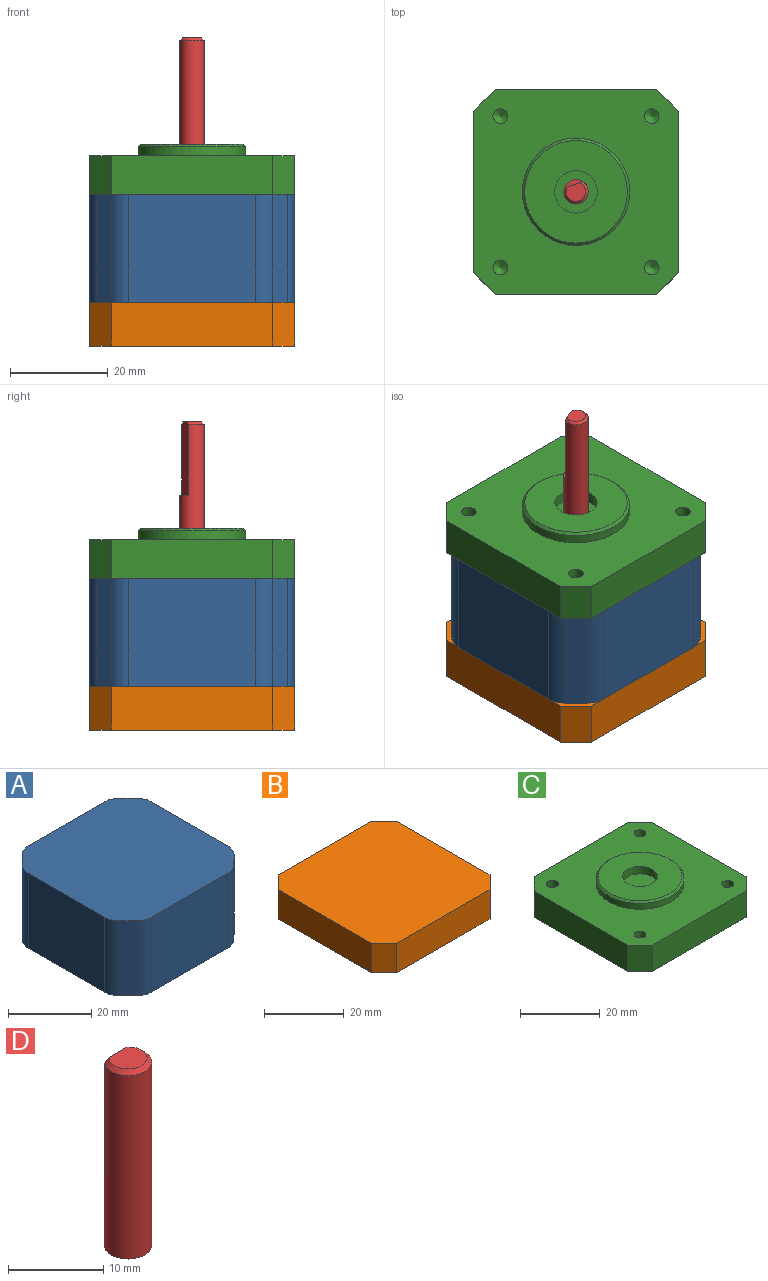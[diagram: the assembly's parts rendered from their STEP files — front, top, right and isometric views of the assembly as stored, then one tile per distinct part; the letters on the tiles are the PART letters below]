
ASSEMBLY  parts=4 mates=3
PART A: 18 faces, bbox 42x42x22 mm
  f0: plane 25.86x22mm, normal (1,0,0), area 568.9mm2, adj f4,f5,f16,f17
  f1: plane 25.86x22mm, normal (0,1,0), area 568.9mm2, adj f4,f5,f12,f13
  f2: plane 25.86x22mm, normal (-1,0,0), area 568.9mm2, adj f4,f5,f10,f11
  f3: plane 25.86x22mm, normal (0,-1,0), area 568.9mm2, adj f4,f5,f14,f15
  f4: plane 42x42mm, normal (0,0,1), area 1687.7mm2, adj f0,f1,f2,f3,f6,f7,f8,f9
  f5: plane 42x42mm, normal (0,0,-1), area 1687.7mm2, adj f0,f1,f2,f3,f6,f7,f8,f9
  f6: plane 22x3.07mm, normal (0.71,-0.71,0), area 95.5mm2, adj f4,f5,f14,f16
  f7: plane 22x3.07mm, normal (0.71,0.71,0), area 95.5mm2, adj f4,f5,f12,f17
  f8: plane 22x3.07mm, normal (-0.71,-0.71,0), area 95.5mm2, adj f4,f5,f10,f15
  f9: plane 22x3.07mm, normal (-0.71,0.71,0), area 95.5mm2, adj f4,f5,f11,f13
  f10: cylinder r=5mm len=22mm, axis (0,0,-1), area 86.4mm2, adj f2,f4,f5,f8
  f11: cylinder r=5mm len=22mm, axis (0,0,-1), area 86.4mm2, adj f2,f4,f5,f9
  f12: cylinder r=5mm len=22mm, axis (0,0,1), area 86.4mm2, adj f1,f4,f5,f7
  f13: cylinder r=5mm len=22mm, axis (0,0,1), area 86.4mm2, adj f1,f4,f5,f9
  f14: cylinder r=5mm len=22mm, axis (0,0,-1), area 86.4mm2, adj f3,f4,f5,f6
  f15: cylinder r=5mm len=22mm, axis (0,0,-1), area 86.4mm2, adj f3,f4,f5,f8
  f16: cylinder r=5mm len=22mm, axis (0,0,1), area 86.4mm2, adj f0,f4,f5,f6
  f17: cylinder r=5mm len=22mm, axis (0,0,1), area 86.4mm2, adj f0,f4,f5,f7
PART B: 10 faces, bbox 42x42x9 mm
  f0: plane 33x9mm, normal (0,-1,0), area 297mm2, adj f4,f5,f8,f9
  f1: plane 33x9mm, normal (1,0,0), area 297mm2, adj f4,f5,f6,f8
  f2: plane 33x9mm, normal (0,1,0), area 297mm2, adj f4,f5,f6,f7
  f3: plane 33x9mm, normal (-1,0,0), area 297mm2, adj f4,f5,f7,f9
  f4: plane 42x42mm, normal (0,0,1), area 1723.5mm2, adj f0,f1,f2,f3,f6,f7,f8,f9
  f5: plane 42x42mm, normal (0,0,-1), area 1723.5mm2, adj f0,f1,f2,f3,f6,f7,f8,f9
  f6: plane 9x4.5mm, normal (0.71,0.71,0), area 57.3mm2, adj f1,f2,f4,f5
  f7: plane 9x4.5mm, normal (-0.71,0.71,0), area 57.3mm2, adj f2,f3,f4,f5
  f8: plane 9x4.5mm, normal (0.71,-0.71,0), area 57.3mm2, adj f0,f1,f4,f5
  f9: plane 9x4.5mm, normal (-0.71,-0.71,0), area 57.3mm2, adj f0,f3,f4,f5
PART C: 23 faces, bbox 42x42x10.3 mm
  f0: plane 33x8mm, normal (0,1,0), area 264mm2, adj f4,f5,f8,f9
  f1: plane 33x8mm, normal (-1,0,0), area 264mm2, adj f4,f5,f7,f9
  f2: plane 33x8mm, normal (0,-1,0), area 264mm2, adj f4,f5,f6,f7
  f3: plane 33x8mm, normal (1,0,0), area 264mm2, adj f4,f5,f6,f8
  f4: plane 42x42mm, normal (0,0,1), area 1315.1mm2, adj f0,f1,f2,f3,f6,f7,f8,f9
  f5: plane 42x42mm, normal (0,0,-1), area 1723.5mm2, adj f0,f1,f2,f3,f6,f7,f8,f9
  f6: plane 8x4.5mm, normal (0.71,-0.71,0), area 50.9mm2, adj f2,f3,f4,f5
  f7: plane 8x4.5mm, normal (-0.71,-0.71,0), area 50.9mm2, adj f1,f2,f4,f5
  f8: plane 8x4.5mm, normal (0.71,0.71,0), area 50.9mm2, adj f0,f3,f4,f5
  f9: plane 8x4.5mm, normal (-0.71,0.71,0), area 50.9mm2, adj f0,f1,f4,f5
  f10: cylinder r=4.35mm len=8.7mm, axis (0,0,-1), area 62.9mm2, adj f12,f13
  f11: cylinder r=11mm len=22mm, axis (0,0,-1), area 124.4mm2, adj f4,f14
  f12: plane 21x21mm, normal (0,0,1), area 286.9mm2, adj f10,f14
  f13: plane 8.7x8.7mm, normal (0,0,1), area 59.4mm2, adj f10
  f14: cone r=10.5mm half-angle=45deg, axis (0,0,-1), area 47.8mm2, adj f11,f12
  f15: cylinder r=1.5mm len=5mm, axis (0,0,1), area 47.1mm2, adj f4,f16
  f16: cone r=0mm half-angle=59deg, axis (0,0,1), area 8.2mm2, adj f15
  f17: cylinder r=1.5mm len=5mm, axis (0,0,1), area 47.1mm2, adj f4,f18
  f18: cone r=0mm half-angle=59deg, axis (0,0,1), area 8.2mm2, adj f17
  f19: cylinder r=1.5mm len=5mm, axis (0,0,1), area 47.1mm2, adj f4,f20
  f20: cone r=0mm half-angle=59deg, axis (0,0,1), area 8.2mm2, adj f19
  f21: cylinder r=1.5mm len=5mm, axis (0,0,1), area 47.1mm2, adj f4,f22
  f22: cone r=0mm half-angle=59deg, axis (0,0,1), area 8.2mm2, adj f21
PART D: 6 faces, bbox 5x5x24.1 mm
  f0: cylinder r=2.5mm len=23.6mm, axis (0,0,-1), area 303.5mm2, adj f2,f3,f4,f5
  f1: plane 4x3.5mm, normal (0,0,1), area 11.7mm2, adj f3,f5
  f2: plane 5x5mm, normal (0,0,-1), area 19.6mm2, adj f0
  f3: plane 15x4mm, normal (0,1,0), area 59.7mm2, adj f0,f1,f4,f5
  f4: plane 4x1mm, normal (0,0,1), area 2.8mm2, adj f0,f3
  f5: cone r=2mm half-angle=45deg, axis (0,0,-1), area 7.3mm2, adj f0,f1,f3
PLACE A t=(0.78,-0.82,-6.41)mm
PLACE B t=(0.78,-0.82,-6.41)mm fixed
PLACE C t=(0.78,-0.82,-6.41)mm
PLACE D rot(axis=(0,0,1),20.1deg) t=(0.78,-0.82,-6.41)mm
MATE fastened A.f4 <-> C.f10  axis (0,0,1) through (0.78,-0.82,24.59)mm
MATE revolute C.f10 <-> D.f0  axis (0,0,1) through (0.78,-0.82,32.59)mm
MATE fastened B.f4 <-> A.f5  axis (0,0,1) through (0.78,-0.82,2.59)mm
